# Revit family: PA653UL lighter
name_source: partatom
category: Generic Models
revit_build: Autodesk Revit Architecture 2012 (Build: 20110309_2315(x64)
units: mm (PartAtom-declared; Revit-internal decimal feet)

## types (1)
- PA653UL lighter
    Dimensions (WxDxH) = 22.8 x 19.4 x 8.2 in. / 580 x 494 x 208mm
    Environmental - Humidity = 20-80% non-condensing
    Environmental - Operating Temperature = 41 deg - 104 degF / -10 deg - 50 degC
    Environmental - Storage = 14 deg - 122 degF / -10 deg - 50 degC
    Fan Noise = 39 dB normal / 33 dB eco
    Input Current = 10.2A - 4.5A
    Installation Orientation = Floor/Front,Floor/Rear,Cuiling/Front,Ceiling/Rear
    Manufacturer = NEC
    Model = PA653UL
    Net Weight = 40.1 lbs / 18.2 kgs
    Optical - Contrast Ratio (up to) = 2,500,000:1 with auto iris
    Optical - Display /Technology = 0.76" LCD w MLA
    Optical - Keystone Correction = +/-40 deg horizontal, +/- 40 deg vertical
    Optical - Laser Life (up to) = 20,000 hours
    Optical - Lens* F-number, f-number NP40ZL = Power zoom/ Power focus, F=2.0 to 2.5, f=13.3 to 18.6mm, 3.6 lbs/ 1.63 kg
    Optical - Lens* F-number, f-number NP41ZL = Power zoom/ Power focus, F=1.7 to 2.0, f=21.8 to 49.8mm, 3.9 lbs/ 1.75 kg
    Optical - Lens* F-number, f-number NP43ZL = Power zoom/ Power focus, F=2.2 to 2.6, f=49.7 to 99.8mm, 3.9 lbs/ 1.77 kg
    Optical - Lens* Focus = Powered
    Optical - Lens* Shift = Powered +0.5/-0.1 vertical, +/-30 horizontal
    Optical - Lens* Zoom = Powered
    Optical - Lens* Zoom Ratio NP40ZL/NP41ZL/NP43ZL = 1.4:1/2.3:1/2.0:1
    Optical - Light Output (lumens) = 6500 normal
    Optical - Projection Angle = 10.3to 10.8 deg tele / 13.7 to 14.5 deg wide
    Optical - Projection Distance = 2.5 to 68.5 ft. / 0.74 to 20.9 m
    Optical - Resolution Maximum = 4K 4096 X 2160
    Optical - Resolution Native = WUXGA 1920 X 1200
    Optical - Screen Size (diagonal) = 50 to 500 in./1.27 to 12.7m, NP40ZL,NP41ZL,NP43ZL,
    Optical - Throw Ratio NP40ZL = 0.79 - 1.11
    Optical - Throw Ratio NP41ZL = 1.30 - 3.02
    Optical - Throw Ratio NP43ZL = 2.88 - 5.93
    Power Consumption (ECO off/ECO Mode/Standby/Standby-Power Saving = 672W / 437W / 0.64W / 0.11
    Power Requirements = 100 - 240V AC, 50/60Hz
    Signal Compatibility/Connectivity - Input Terminals RGB1 (analog) = VGA 15 pin D-sub, Component video using ADP-CV1E adapter
    Signal Compatibility/Connectivity - Input Terminals RGB2 (digital) = HDMI (V2.0) w/HDCP (V1.4/2.2)
    Signal Compatibility/Connectivity - Input Terminals RGB3 (digital) = HDMI (V2.0) w/HDCP (V1.4/2.2)
    Signal Compatibility/Connectivity - Input Terminals RGB4 (digital) = DisplayPort w/HDCP (V1.4)
    Signal Compatibility/Connectivity - Input Terminals RGB5 (digital) = HDBaseT w/HDCP (V1.4/2.2)
    Signal Compatibility/Connectivity - Macintosh Compatibility = Yes
    Signal Compatibility/Connectivity - Output Terminals 3D Sync Line = 3Pin D
    Signal Compatibility/Connectivity - Output Terminals Audio Out = Stereo Mini Jack
    Signal Compatibility/Connectivity - Output Terminals Monitor Out = HDBaseT w/HDCP (V1.4/2.2)
    Signal Compatibility/Connectivity - PC Signal Compatibility = VGA, SVGA,XGA,SXGA,+, UXGA,WUXGA
    Signal Compatibility/Connectivity - SD/HD Video Signal Compatibility = 4K, 1080p, 1080i, 720p, 576p, 576i, 480p, 480i
    Signal Compatibility/Connectivity - Supported Video Standards = NTSC, NTSC4.43, PAL, PAL-60, PAL-M, PAL-N, SECAM
    Signal Compatibility/Connectivity - Sync Compatibility = Separate Sync / Composite Sync/ Sync on G
    URL = www.necdisplay.com

## geometry (parser evidence)
native form markers: Sweep x1
no freeform markers — native parametric forms only
